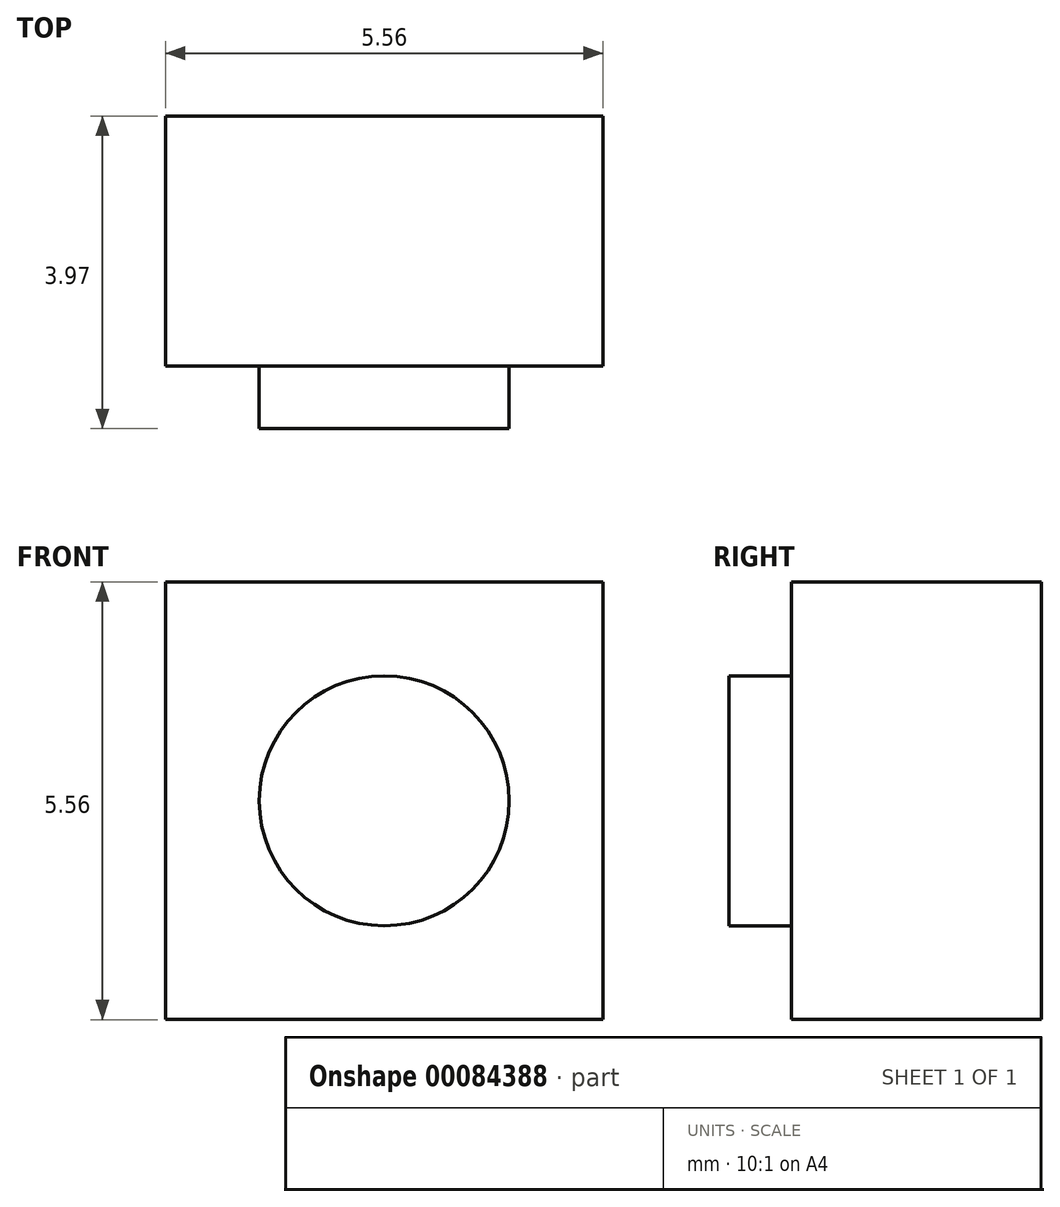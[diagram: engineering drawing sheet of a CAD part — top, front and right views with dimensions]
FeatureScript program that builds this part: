
annotation { "Feature Type Name" : "Feature", "Feature Type Description" : "" }
export const myFeature = defineFeature(function(context is Context, id is Id, definition is map)
    precondition{}
    {
        {
            var Q0;
            Q0=qCreatedBy(makeId("Front.planeOp"),FACE);
            var sketch = newSketch(context, id + "F0", { "sketchPlane" : qUnion([Q0])});
            skLineSegment(sketch, "E0.bottom", {"start": v(2.78, 2.78) * mm, "end": v(-2.78, 2.78) * mm});
            skLineSegment(sketch, "E0.top", {"start": v(2.78, -2.78) * mm, "end": v(-2.78, -2.78) * mm});
            skLineSegment(sketch, "E0.left", {"start": v(2.78, 2.78) * mm, "end": v(2.78, -2.78) * mm});
            skLineSegment(sketch, "E0.right", {"start": v(-2.78, 2.78) * mm, "end": v(-2.78, -2.78) * mm});
            skPoint(sketch, "E0.middle", {"position": v(0, 0) * mm});
            skCircle(sketch, "E1", {"center": v(0, 0) * mm, "radius": 1.59 * mm});
            skSolve(sketch);
        }
        {
            var Q0;
            Q0 = qSketchRegion(id + "F0", true);
            var Q1;
            Q1=makeQuery(id+"F0.imprint","IMPRINT",FACE,{"disambiguationData":[TD([[makeQuery(id+"F0.imprint","IMPRINT",EDGE,{"derivedFrom":sQuery(id+"F0.wireOp",EDGE,"E1")}),1.0]])]});
            extrude(context, id + "F1", {"entities" : qUnion([Q0, Q1]), "depth" : 3.17 * mm});
        }
        {
            var Q0;
            Q0=makeQuery(id+"F1.opExtrude","CAP_FACE",FACE,{"disambiguationData":[OSD([sQuery(id+"F0.wireOp",EDGE,"E0.bottom"),sQuery(id+"F0.wireOp",EDGE,"E0.top"),sQuery(id+"F0.wireOp",EDGE,"E0.left"),sQuery(id+"F0.wireOp",EDGE,"E0.right")])],"isStart":false});
            var sketch = newSketch(context, id + "F2", { "sketchPlane" : qUnion([Q0])});
            skCircle(sketch, "E2", {"center": v(0, 0) * mm, "radius": 1.59 * mm});
            skSolve(sketch);
        }
        {
            var Q0;
            Q0 = qSketchRegion(id + "F2", true);
            extrude(context, id + "F3", {"entities" : qUnion([Q0]), "operationType" : NewBodyOperationType.ADD, "depth" : 0.8 * mm});
        }
    });
